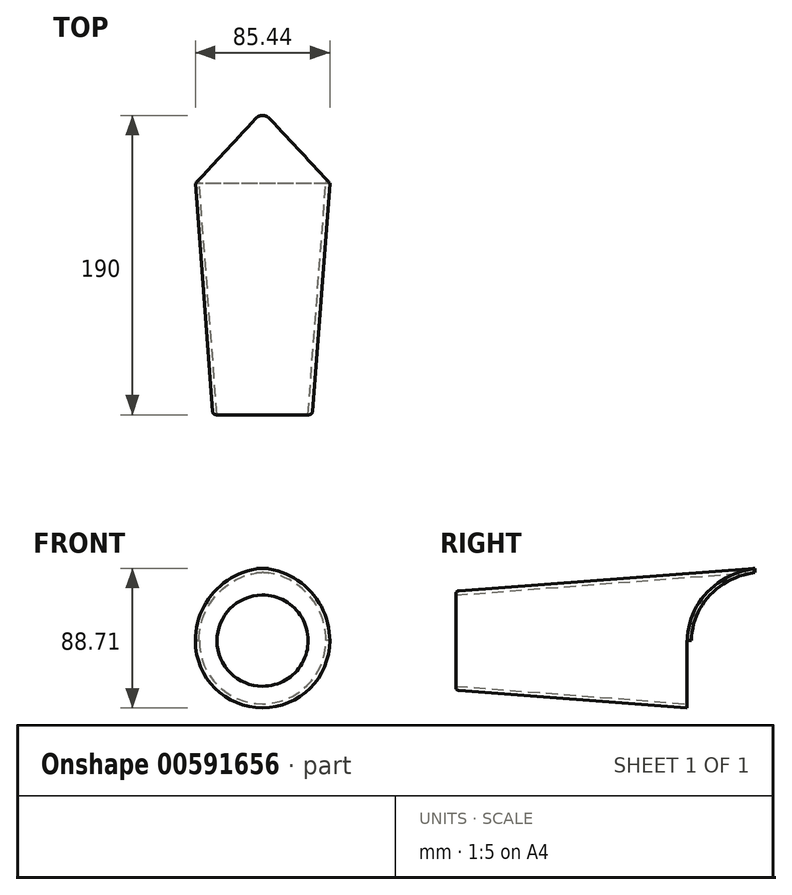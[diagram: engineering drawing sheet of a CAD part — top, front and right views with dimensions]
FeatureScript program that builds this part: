
annotation { "Feature Type Name" : "Feature", "Feature Type Description" : "" }
export const myFeature = defineFeature(function(context is Context, id is Id, definition is map)
    precondition{}
    {
        {
            var Q0;
            Q0=qCreatedBy(makeId("Front.planeOp"),FACE);
            var sketch = newSketch(context, id + "F0", { "sketchPlane" : qUnion([Q0])});
            skCircle(sketch, "E0", {"center": v(0, 0) * mm, "radius": 31.5 * mm});
            skSolve(sketch);
        }
        {
            var Q0;
            Q0=qCreatedBy(makeId("Front.planeOp"),FACE);
            cPlane(context, id + "F1", {"entities" : qUnion([Q0]), "cplaneType" : CPlaneType.OFFSET, "offset" : 190 * mm, "oppositeDirection" : true, "width" : 152.4 * mm, "height" : 152.4 * mm});
        }
        {
            var Q0;
            Q0=qCreatedBy(id+"F1.planeOp",FACE);
            var sketch = newSketch(context, id + "F2", { "sketchPlane" : qUnion([Q0])});
            skCircle(sketch, "E1", {"center": v(0, 0) * mm, "radius": 46 * mm});
            skSolve(sketch);
        }
        {
            var Q0;
            Q0=makeQuery(id+"F2.imprint","IMPRINT",FACE,{"disambiguationData":[TD([[makeQuery(id+"F2.imprint","IMPRINT",EDGE,{"derivedFrom":sQuery(id+"F2.wireOp",EDGE,"E1")}),1.0]])]});
            var Q1;
            Q1=makeQuery(id+"F0.imprint","IMPRINT",FACE,{"disambiguationData":[TD([[makeQuery(id+"F0.imprint","IMPRINT",EDGE,{"derivedFrom":sQuery(id+"F0.wireOp",EDGE,"E0")}),1.0]])]});
            loft(context, id + "F3", {"sheetProfilesArray" : [{ "sheetProfileEntities" : qUnion([Q0]) }, { "sheetProfileEntities" : qUnion([Q1]) }]});
        }
        {
            var Q0;
            Q0=makeQuery(id+"F3.opLoft","CAP_FACE",FACE,{"disambiguationData":[OSD([makeQuery(id+"F0.imprint","IMPRINT",FACE,{"disambiguationData":[TD([[makeQuery(id+"F0.imprint","IMPRINT",EDGE,{"derivedFrom":sQuery(id+"F0.wireOp",EDGE,"E0")}),1.0]])]})])],"isStart":true});
            var Q1;
            Q1=makeQuery(id+"F3.opLoft","CAP_FACE",FACE,{"disambiguationData":[OSD([makeQuery(id+"F2.imprint","IMPRINT",FACE,{"disambiguationData":[TD([[makeQuery(id+"F2.imprint","IMPRINT",EDGE,{"derivedFrom":sQuery(id+"F2.wireOp",EDGE,"E1")}),1.0]])]})])],"isStart":true});
            shell(context, id + "F4", {"entities" : qUnion([Q0, Q1]), "thickness" : 2.54 * mm});
        }
        {
            var Q0;
            Q0=qCreatedBy(makeId("Top.planeOp"),FACE);
            var sketch = newSketch(context, id + "F5", { "sketchPlane" : qUnion([Q0])});
            skLineSegment(sketch, "E2", {"start": v(-43.85, 145.54) * mm, "end": v(0, 192.87) * mm});
            skLineSegment(sketch, "E3", {"start": v(0, 192.87) * mm, "end": v(-50.45, 192.87) * mm});
            skLineSegment(sketch, "E4", {"start": v(-50.45, 192.87) * mm, "end": v(-43.85, 145.54) * mm});
            skLineSegment(sketch, "E5", {"start": v(44.23, 145.54) * mm, "end": v(0, 192.87) * mm});
            skLineSegment(sketch, "E6", {"start": v(49.81, 192.87) * mm, "end": v(44.23, 145.54) * mm});
            skLineSegment(sketch, "E7", {"start": v(49.81, 192.87) * mm, "end": v(0, 192.87) * mm});
            skSolve(sketch);
        }
        {
            var Q0;
            Q0 = qSketchRegion(id + "F5", true);
            extrude(context, id + "F6", {"entities" : qUnion([Q0]), "operationType" : NewBodyOperationType.REMOVE, "depth" : 68.58 * mm, "offsetDistance" : 25.4 * mm});
        }
        {
            var Q0;
            Q0=qCreatedBy(makeId("Right.planeOp"),FACE);
            var sketch = newSketch(context, id + "F7", { "sketchPlane" : qUnion([Q0])});
            skLineSegment(sketch, "E8.bottom", {"start": v(190.56, 0) * mm, "end": v(146.83, 0) * mm});
            skLineSegment(sketch, "E8.top", {"start": v(190.56, -56.1) * mm, "end": v(146.83, -56.1) * mm});
            skLineSegment(sketch, "E8.left", {"start": v(190.56, 0) * mm, "end": v(190.56, -56.1) * mm});
            skLineSegment(sketch, "E8.right", {"start": v(146.83, 0) * mm, "end": v(146.83, -56.1) * mm});
            skSolve(sketch);
        }
        {
            var Q0;
            Q0 = qSketchRegion(id + "F7", true);
            extrude(context, id + "F8", {"entities" : qUnion([Q0]), "operationType" : NewBodyOperationType.REMOVE, "endBound" : BoundingType.SYMMETRIC, "depth" : 132.08 * mm, "offsetDistance" : 25.4 * mm});
        }
        {
            var Q0;
            Q0=makeQuery(id+"F6.boolean.opBoolean","INTERSECT",EDGE,{"derivedFrom":[makeQuery(id+"F3.opLoft","CAP_FACE",FACE,{"disambiguationData":[OSD([makeQuery(id+"F2.imprint","IMPRINT",FACE,{"disambiguationData":[TD([[makeQuery(id+"F2.imprint","IMPRINT",EDGE,{"derivedFrom":sQuery(id+"F2.wireOp",EDGE,"E1")}),1.0]])]})])],"isStart":true}),makeQuery(id+"F6.opExtrude","SWEPT_FACE",FACE,{"disambiguationData":[OSD([sQuery(id+"F5.wireOp",EDGE,"E2")])]})]});
            var Q1;
            Q1=makeQuery(id+"F6.boolean.opBoolean","INTERSECT",EDGE,{"derivedFrom":[makeQuery(id+"F3.opLoft","CAP_FACE",FACE,{"disambiguationData":[OSD([makeQuery(id+"F2.imprint","IMPRINT",FACE,{"disambiguationData":[TD([[makeQuery(id+"F2.imprint","IMPRINT",EDGE,{"derivedFrom":sQuery(id+"F2.wireOp",EDGE,"E1")}),1.0]])]})])],"isStart":true}),makeQuery(id+"F6.opExtrude","SWEPT_FACE",FACE,{"disambiguationData":[OSD([sQuery(id+"F5.wireOp",EDGE,"E5")])]})]});
            fillet(context, id + "F9", {"entities" : qUnion([Q0, Q1]), "radius" : 5.08 * mm, "tangentPropagation" : true, "allowEdgeOverflow" : false});
        }
        {
            var Q0;
            Q0=makeQuery(id+"F3.opLoft","MID_CAP_EDGE",EDGE,{"disambiguationData":[OSD([sQuery(id+"F0.wireOp",EDGE,"E0")])],"capPos":1.0});
            fillet(context, id + "F10", {"entities" : qUnion([Q0]), "radius" : 2.1 * mm, "tangentPropagation" : true, "allowEdgeOverflow" : false});
        }
    });
